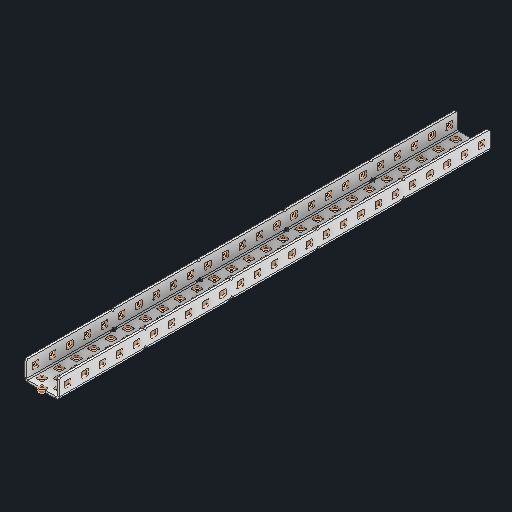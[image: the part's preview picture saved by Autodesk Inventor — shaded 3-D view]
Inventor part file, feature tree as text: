
AUTODESK INVENTOR PART (.ipt)
format: ipt  version: 2025 (Build 290162000, 162)  size: 2,051,072 bytes
history: native  units: in
note: dims shown in document units (in); Inventor stores cm internally (conversion verified against a paired STEP export)
features: other x256, sketch x5, sheet_metal_op x1
ambient origin geometry x8: Origin, YZ Plane, XZ Plane, XY Plane, X Axis, Y Axis, Z Axis, Center Point
bodies: Solid1 (feature_tree)
feature tree (262):
  other  "Alu C 1x2x1x25.ipt"
  other  "Solid1::Alu C 1x2x1x25.ipt"
  other  "TaggingFeature1"
  sketch  "Sketch1"  dims[d0=0.3937in]
  sketch  "Sketch2"  dims[d1=0.0625in]
  sketch  "Sketch3"
  other  "Flange Pattern Sketch"
  sketch  "Sketch9"
  sheet_metal_op  "Body Pattern Sketch"
  other  "Arc Length"
  sketch  "Sketch14"
  other  "Flange Pattern Plane"
  other  "Srf1"
  other  "Srf2"
  other  "Srf3"
  other  "Srf4"
  other  "Srf5"
  other  "Srf6"
  other  "Srf7"
  other  "Srf8"
  other  "Srf9"
  other  "Srf10"
  other  "Srf11"
  other  "Srf12"
  other  "Srf13"
  other  "Srf14"
  other  "Srf15"
  other  "Srf16"
  other  "Srf17"
  other  "Srf18"
  other  "Srf19"
  other  "Srf20"
  other  "Srf21"
  other  "Srf22"
  other  "Srf23"
  other  "Srf24"
  other  "Srf25"
  other  "Srf26"
  other  "Srf27"
  other  "Srf28"
  other  "Srf29"
  other  "Srf30"
  other  "Srf31"
  other  "Srf32"
  other  "Srf33"
  other  "Srf34"
  other  "Srf35"
  other  "Srf36"
  other  "Srf37"
  other  "Srf38"
  other  "Srf39"
  other  "Srf40"
  other  "Srf41"
  other  "Srf42"
  other  "Srf43"
  other  "Srf44"
  other  "Srf45"
  other  "Srf46"
  other  "Srf47"
  other  "Srf48"
  other  "Srf49"
  other  "Srf50"
  other  "Srf51"
  other  "Srf52"
  other  "Srf53"
  other  "Srf54"
  other  "Srf55"
  other  "Srf56"
  other  "Srf57"
  other  "Srf58"
  other  "Srf59"
  other  "Srf60"
  other  "Srf61"
  other  "Srf62"
  other  "Srf63"
  other  "Srf64"
  other  "Srf65"
  other  "Srf66"
  other  "Srf67"
  other  "Srf68"
  other  "Srf69"
  other  "Srf70"
  other  "Srf71"
  other  "Srf72"
  other  "Srf73"
  other  "Srf74"
  other  "Srf75"
  other  "Srf76"
  other  "Srf77"
  other  "Srf78"
  other  "Srf79"
  other  "Srf80"
  other  "Srf81"
  other  "Srf82"
  other  "Srf83"
  other  "Srf84"
  other  "Srf85"
  other  "Srf86"
  other  "Srf87"
  other  "Srf88"
  other  "Srf89"
  other  "Srf90"
  other  "Srf91"
  other  "Srf92"
  other  "Srf93"
  other  "Srf94"
  other  "Srf95"
  other  "Srf96"
  other  "Srf97"
  other  "Srf98"
  other  "Srf99"
  other  "Srf100"
  other  "Srf101"
  other  "Srf102"
  other  "Srf103"
  other  "Srf104"
  other  "Srf105"
  other  "Srf106"
  other  "Srf107"
  other  "Srf108"
  other  "Srf109"
  other  "Srf110"
  other  "Srf111"
  other  "Srf112"
  other  "Srf113"
  other  "Srf114"
  other  "Srf115"
  other  "Srf116"
  other  "Srf117"
  other  "Srf118"
  other  "Srf119"
  other  "Srf120"
  other  "Srf121"
  other  "Srf122"
  other  "Srf123"
  other  "Srf124"
  other  "Srf125"
  other  "Srf1::Derived"
  other  "Srf2::Derived"
  other  "Srf823::Derived"
  other  "Srf824::Derived"
  other  "Srf825::Derived"
  other  "Srf826::Derived"
  other  "Srf827::Derived"
  other  "Srf828::Derived"
  other  "Srf829::Derived"
  other  "Srf922::Derived"
  other  "Srf923::Derived"
  other  "Srf924::Derived"
  other  "Srf925::Derived"
  other  "Srf926::Derived"
  other  "Srf1143::Derived"
  other  "Srf1144::Derived"
  other  "Srf1145::Derived"
  other  "Srf1146::Derived"
  other  "Srf1147::Derived"
  other  "Srf1148::Derived"
  other  "Srf1149::Derived"
  other  "Srf1150::Derived"
  other  "Srf1151::Derived"
  other  "Srf1152::Derived"
  other  "Srf1153::Derived"
  other  "Srf1154::Derived"
  other  "Srf1155::Derived"
  other  "Srf1156::Derived"
  other  "Srf1157::Derived"
  other  "Srf1158::Derived"
  other  "Srf1159::Derived"
  other  "Srf1160::Derived"
  other  "Srf1161::Derived"
  other  "Srf1162::Derived"
  other  "Srf1163::Derived"
  other  "Srf1164::Derived"
  other  "Srf1165::Derived"
  other  "Srf1166::Derived"
  other  "Srf1167::Derived"
  other  "Srf1168::Derived"
  other  "Srf1169::Derived"
  other  "Srf1170::Derived"
  other  "Srf1171::Derived"
  other  "Srf1172::Derived"
  other  "Srf1173::Derived"
  other  "Srf1174::Derived"
  other  "Srf1175::Derived"
  other  "Srf1176::Derived"
  other  "Srf1177::Derived"
  other  "Srf1178::Derived"
  other  "Srf91::Derived"
  other  "Srf92::Derived"
  other  "Srf856::Derived"
  other  "Srf857::Derived"
  other  "Srf858::Derived"
  other  "Srf859::Derived"
  other  "Srf860::Derived"
  other  "Srf861::Derived"
  other  "Srf862::Derived"
  other  "Srf959::Derived"
  other  "Srf960::Derived"
  other  "Srf961::Derived"
  other  "Srf962::Derived"
  other  "Srf963::Derived"
  other  "Srf1199::Derived"
  other  "Srf1200::Derived"
  other  "Srf1201::Derived"
  other  "Srf1202::Derived"
  other  "Srf1203::Derived"
  other  "Srf1204::Derived"
  other  "Srf1205::Derived"
  other  "Srf1206::Derived"
  other  "Srf1207::Derived"
  other  "Srf1208::Derived"
  other  "Srf1209::Derived"
  other  "Srf1210::Derived"
  other  "Srf1211::Derived"
  other  "Srf1212::Derived"
  other  "Srf1213::Derived"
  other  "Srf1214::Derived"
  other  "Srf1215::Derived"
  other  "Srf1216::Derived"
  other  "Srf1217::Derived"
  other  "Srf1218::Derived"
  other  "Srf1219::Derived"
  other  "Srf1220::Derived"
  other  "Srf1221::Derived"
  other  "Srf1222::Derived"
  other  "Srf1223::Derived"
  other  "Srf1224::Derived"
  other  "Srf1225::Derived"
  other  "Srf1226::Derived"
  other  "Srf1227::Derived"
  other  "Srf1228::Derived"
  other  "Srf1229::Derived"
  other  "Srf1230::Derived"
  other  "Srf1231::Derived"
  other  "Srf1232::Derived"
  other  "Srf1233::Derived"
  other  "Srf1234::Derived"
  other  "Srf786::Derived"
  other  "Srf889::Derived"
  other  "Srf890::Derived"
  other  "Srf891::Derived"
  other  "Srf892::Derived"
  other  "Srf893::Derived"
  other  "Srf894::Derived"
  other  "Srf895::Derived"
  other  "Srf896::Derived"
  other  "Srf996::Derived"
  other  "Srf997::Derived"
  other  "Srf998::Derived"
  other  "Srf999::Derived"
  other  "Srf1000::Derived"
  other  "Srf1255::Derived"
  other  "Srf1256::Derived"
  other  "Srf1257::Derived"
  other  "Srf1258::Derived"
  other  "Srf1259::Derived"
  other  "Srf1260::Derived"
  other  "Srf1261::Derived"
  other  "Srf1262::Derived"
  other  "Srf1263::Derived"
  other  "Srf1264::Derived"
  other  "Srf1265::Derived"
